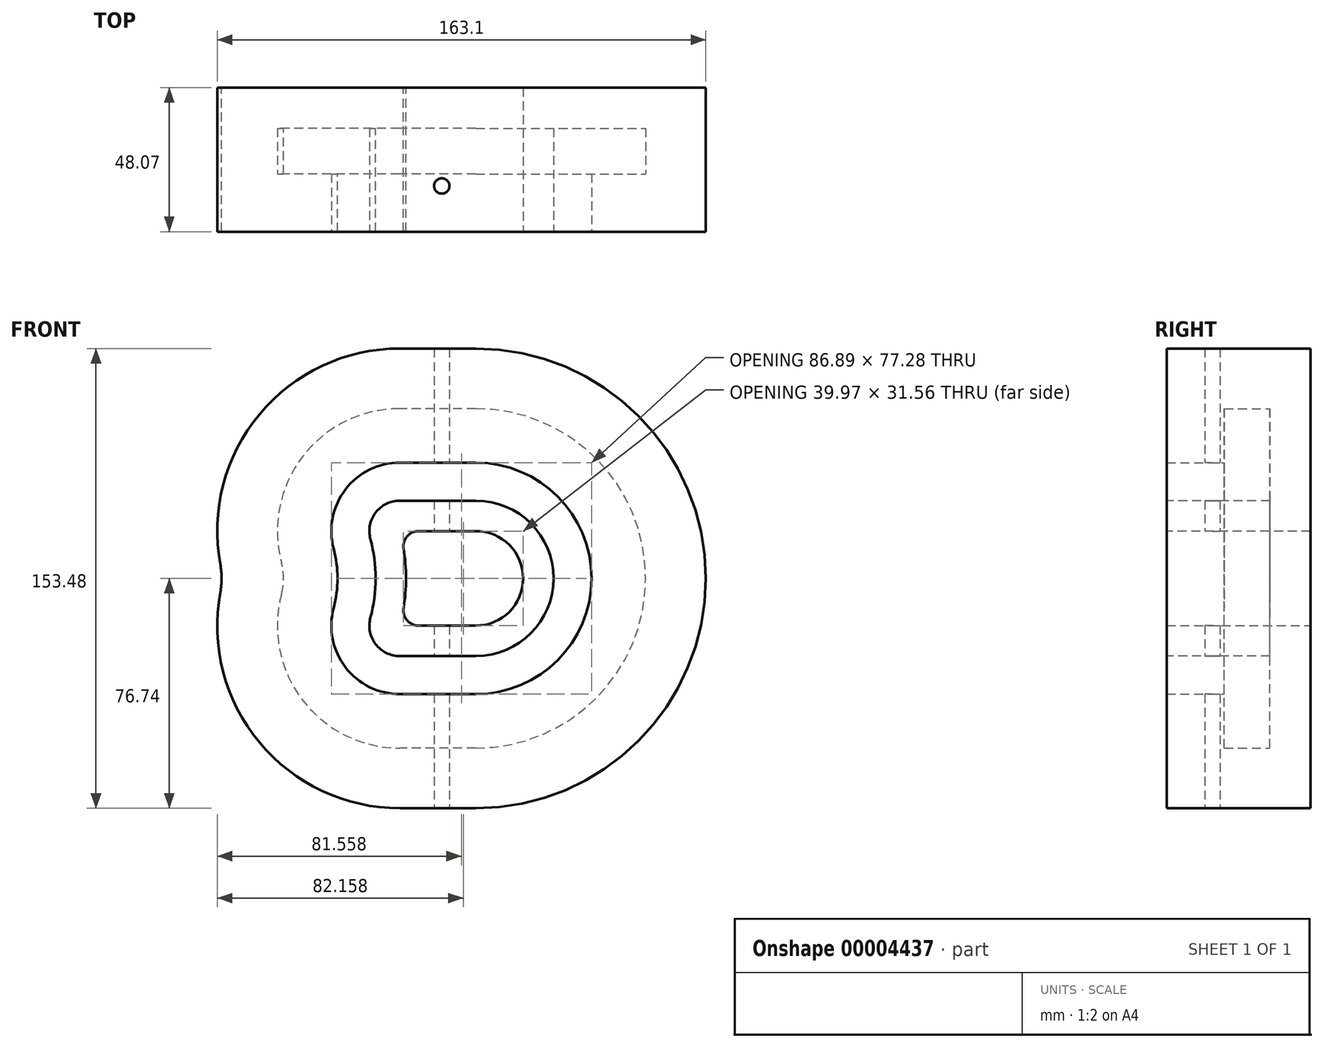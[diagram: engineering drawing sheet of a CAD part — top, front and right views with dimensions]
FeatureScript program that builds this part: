
annotation { "Feature Type Name" : "Feature", "Feature Type Description" : "" }
export const myFeature = defineFeature(function(context is Context, id is Id, definition is map)
    precondition{}
    {
        {
            var Q0;
            Q0=qCreatedBy(makeId("Top.planeOp"),FACE);
            var sketch = newSketch(context, id + "F0", { "sketchPlane" : qUnion([Q0])});
            skLineSegment(sketch, "E0", {"start": v(0, 0) * mm, "end": v(38.1, 0) * mm});
            skLineSegment(sketch, "E1", {"start": v(38.1, 0) * mm, "end": v(38.1, 19.26) * mm});
            skLineSegment(sketch, "E2", {"start": v(38.1, 19.26) * mm, "end": v(20.08, 19.26) * mm});
            skLineSegment(sketch, "E3", {"start": v(20.08, 19.26) * mm, "end": v(20.08, 34.5) * mm});
            skLineSegment(sketch, "E4", {"start": v(20.08, 34.5) * mm, "end": v(50.8, 34.5) * mm});
            skLineSegment(sketch, "E5", {"start": v(50.8, 34.5) * mm, "end": v(50.8, 0) * mm});
            skLineSegment(sketch, "E6", {"start": v(50.8, 0) * mm, "end": v(60.96, 0) * mm});
            skLineSegment(sketch, "E7", {"start": v(60.96, 0) * mm, "end": v(60.96, 48.07) * mm});
            skLineSegment(sketch, "E8", {"start": v(60.96, 48.07) * mm, "end": v(0, 48.07) * mm});
            skLineSegment(sketch, "E9", {"start": v(0, 48.07) * mm, "end": v(0, 0) * mm});
            skSolve(sketch);
        }
        {
            var Q0;
            Q0=makeQuery(id+"F0.imprint","IMPRINT",FACE,{"disambiguationData":[TD([[makeQuery(id+"F0.imprint","IMPRINT",EDGE,{"derivedFrom":sQuery(id+"F0.wireOp",EDGE,"E0")}),1.0]])]});
            var Q1;
            Q1=sQuery(id+"F0.wireOp",EDGE,"E9");
            revolve(context, id + "F1", {"entities" : qUnion([Q0]), "axis" : qUnion([Q1]), "revolveType" : RevolveType.SYMMETRIC, "angle" : 30 * degree});
        }
        {
            var Q0;
            Q0=makeQuery(id+"F1.opRevolve","CAP_FACE",FACE,{"disambiguationData":[OSD([sQuery(id+"F0.wireOp",EDGE,"E0"),sQuery(id+"F0.wireOp",EDGE,"E1"),sQuery(id+"F0.wireOp",EDGE,"E2"),sQuery(id+"F0.wireOp",EDGE,"E3"),sQuery(id+"F0.wireOp",EDGE,"E4"),sQuery(id+"F0.wireOp",EDGE,"E5"),sQuery(id+"F0.wireOp",EDGE,"E6"),sQuery(id+"F0.wireOp",EDGE,"E7"),sQuery(id+"F0.wireOp",EDGE,"E8"),sQuery(id+"F0.wireOp",EDGE,"E9")])],"isStart":false});
            var Q1;
            Q1=makeQuery(id+"F1.opRevolve","CAP_EDGE",EDGE,{"disambiguationData":[OSD([sQuery(id+"F0.wireOp",EDGE,"E7")])],"isStart":false});
            revolve(context, id + "F2", {"operationType" : NewBodyOperationType.ADD, "entities" : qUnion([Q0]), "axis" : qUnion([Q1]), "revolveType" : RevolveType.ONE_DIRECTION, "angle" : 105 * degree});
        }
        {
            var Q0;
            Q0=makeQuery(id+"F1.opRevolve","CAP_FACE",FACE,{"disambiguationData":[OSD([sQuery(id+"F0.wireOp",EDGE,"E0"),sQuery(id+"F0.wireOp",EDGE,"E1"),sQuery(id+"F0.wireOp",EDGE,"E2"),sQuery(id+"F0.wireOp",EDGE,"E3"),sQuery(id+"F0.wireOp",EDGE,"E4"),sQuery(id+"F0.wireOp",EDGE,"E5"),sQuery(id+"F0.wireOp",EDGE,"E6"),sQuery(id+"F0.wireOp",EDGE,"E7"),sQuery(id+"F0.wireOp",EDGE,"E8"),sQuery(id+"F0.wireOp",EDGE,"E9")])],"isStart":true});
            var Q1;
            Q1=makeQuery(id+"F1.opRevolve","CAP_EDGE",EDGE,{"disambiguationData":[OSD([sQuery(id+"F0.wireOp",EDGE,"E7")])],"isStart":true});
            revolve(context, id + "F3", {"operationType" : NewBodyOperationType.ADD, "entities" : qUnion([Q0]), "axis" : qUnion([Q1]), "revolveType" : RevolveType.ONE_DIRECTION, "oppositeDirection" : true, "angle" : 105 * degree});
        }
        {
            var Q0;
            {var subQ0=sQuery(id+"F0.wireOp",EDGE,"E9");Q0=makeQuery(id+"F3.boolean.opBoolean","MERGE",EDGE,{"derivedFrom":[makeQuery(id+"F2.boolean.opBoolean","MERGE",EDGE,{"derivedFrom":[makeQuery(id+"F1.opRevolve","CAP_EDGE",EDGE,{"disambiguationData":[OSD([subQ0])],"isStart":true}),makeQuery(id+"F2.opRevolve","CAP_EDGE",EDGE,{"disambiguationData":[OSD([subQ0])],"isStart":true})]}),makeQuery(id+"F3.opRevolve","CAP_EDGE",EDGE,{"disambiguationData":[OSD([subQ0])],"isStart":true})]});}
            fillet(context, id + "F4", {"entities" : qUnion([Q0]), "radius" : 25.4 * mm, "tangentPropagation" : true, "allowEdgeOverflow" : false});
        }
        {
            var Q0;
            Q0=makeQuery(id+"F3.opRevolve","CAP_FACE",FACE,{"disambiguationData":[OSD([sQuery(id+"F0.wireOp",EDGE,"E0"),sQuery(id+"F0.wireOp",EDGE,"E1"),sQuery(id+"F0.wireOp",EDGE,"E2"),sQuery(id+"F0.wireOp",EDGE,"E3"),sQuery(id+"F0.wireOp",EDGE,"E4"),sQuery(id+"F0.wireOp",EDGE,"E5"),sQuery(id+"F0.wireOp",EDGE,"E6"),sQuery(id+"F0.wireOp",EDGE,"E7"),sQuery(id+"F0.wireOp",EDGE,"E8"),sQuery(id+"F0.wireOp",EDGE,"E9")])],"isStart":false});
            var Q1;
            Q1=makeQuery(id+"F2.opRevolve","CAP_FACE",FACE,{"disambiguationData":[OSD([sQuery(id+"F0.wireOp",EDGE,"E0"),sQuery(id+"F0.wireOp",EDGE,"E1"),sQuery(id+"F0.wireOp",EDGE,"E2"),sQuery(id+"F0.wireOp",EDGE,"E3"),sQuery(id+"F0.wireOp",EDGE,"E4"),sQuery(id+"F0.wireOp",EDGE,"E5"),sQuery(id+"F0.wireOp",EDGE,"E6"),sQuery(id+"F0.wireOp",EDGE,"E7"),sQuery(id+"F0.wireOp",EDGE,"E8"),sQuery(id+"F0.wireOp",EDGE,"E9")])],"isStart":false});
            extrude(context, id + "F5", {"entities" : qUnion([Q0, Q1]), "operationType" : NewBodyOperationType.ADD, "depth" : 25.4 * mm});
        }
        {
            var Q0;
            {var subQ0=sQuery(id+"F0.wireOp",EDGE,"E7");var subQ1=makeQuery(id+"F3.boolean.opBoolean","MERGE",EDGE,{"derivedFrom":[makeQuery(id+"F1.opRevolve","CAP_EDGE",EDGE,{"disambiguationData":[OSD([subQ0])],"isStart":true}),makeQuery(id+"F3.opRevolve","CAP_EDGE",EDGE,{"disambiguationData":[OSD([subQ0])],"isStart":true})]});Q0=makeQuery(id+"F5.boolean.opBoolean","MERGE",EDGE,{"derivedFrom":[subQ1,makeQuery(id+"F5.opExtrude","CAP_EDGE",EDGE,{"disambiguationData":[OSD([subQ0]),TDD([subQ1])],"isStart":true})]});}
            var Q1;
            {var subQ0=sQuery(id+"F0.wireOp",EDGE,"E7");var subQ1=makeQuery(id+"F2.boolean.opBoolean","MERGE",EDGE,{"derivedFrom":[makeQuery(id+"F1.opRevolve","CAP_EDGE",EDGE,{"disambiguationData":[OSD([subQ0])],"isStart":false}),makeQuery(id+"F2.opRevolve","CAP_EDGE",EDGE,{"disambiguationData":[OSD([subQ0])],"isStart":true})]});Q1=makeQuery(id+"F5.boolean.opBoolean","MERGE",EDGE,{"derivedFrom":[subQ1,makeQuery(id+"F5.opExtrude","CAP_EDGE",EDGE,{"disambiguationData":[OSD([subQ0]),TDD([subQ1])],"isStart":true})]});}
            fillet(context, id + "F6", {"entities" : qUnion([Q0, Q1]), "radius" : 5.08 * mm, "tangentPropagation" : true, "allowEdgeOverflow" : false});
        }
        {
            var Q0;
            {var subQ0=sQuery(id+"F0.wireOp",EDGE,"E0");var subQ1=sQuery(id+"F0.wireOp",EDGE,"E1");var subQ2=sQuery(id+"F0.wireOp",EDGE,"E2");var subQ3=sQuery(id+"F0.wireOp",EDGE,"E3");var subQ4=sQuery(id+"F0.wireOp",EDGE,"E4");var subQ5=sQuery(id+"F0.wireOp",EDGE,"E5");var subQ6=sQuery(id+"F0.wireOp",EDGE,"E6");var subQ7=sQuery(id+"F0.wireOp",EDGE,"E7");var subQ8=sQuery(id+"F0.wireOp",EDGE,"E8");var subQ9=sQuery(id+"F0.wireOp",EDGE,"E9");Q0=makeQuery(id+"F5.opExtrude","CAP_FACE",FACE,{"disambiguationData":[OSD([subQ0,subQ1,subQ2,subQ3,subQ4,subQ5,subQ6,subQ7,subQ8,subQ9]),TDD([makeQuery(id+"F2.opRevolve","CAP_FACE",FACE,{"disambiguationData":[OSD([subQ0,subQ1,subQ2,subQ3,subQ4,subQ5,subQ6,subQ7,subQ8,subQ9])],"isStart":false})])],"isStart":false});}
            var sketch = newSketch(context, id + "F7", { "sketchPlane" : qUnion([Q0])});
            skLineSegment(sketch, "E10", {"start": v(0, 0) * mm, "end": v(61.35, 0) * mm});
            skLineSegment(sketch, "E11.0.0", {"start": v(48.07, 76.74) * mm, "end": v(0, 76.74) * mm});
            skLineSegment(sketch, "E11.0.1", {"start": v(0, 76.74) * mm, "end": v(0, 38.64) * mm});
            skLineSegment(sketch, "E11.0.2", {"start": v(0, 38.64) * mm, "end": v(19.26, 38.64) * mm});
            skLineSegment(sketch, "E11.0.3", {"start": v(19.26, 38.64) * mm, "end": v(19.26, 56.66) * mm});
            skLineSegment(sketch, "E11.0.4", {"start": v(19.26, 56.66) * mm, "end": v(34.5, 56.66) * mm});
            skLineSegment(sketch, "E11.0.5", {"start": v(34.5, 56.66) * mm, "end": v(34.5, 25.94) * mm});
            skLineSegment(sketch, "E11.0.6", {"start": v(34.5, 25.94) * mm, "end": v(0, 25.94) * mm});
            skLineSegment(sketch, "E11.0.7", {"start": v(0, 25.94) * mm, "end": v(0, 15.78) * mm});
            skLineSegment(sketch, "E11.0.8", {"start": v(0, 15.78) * mm, "end": v(48.07, 15.78) * mm});
            skLineSegment(sketch, "E11.0.9", {"start": v(48.07, 15.78) * mm, "end": v(48.07, 76.74) * mm});
            skSolve(sketch);
        }
        {
            var Q0;
            Q0 = qSketchRegion(id + "F7", true);
            var Q1;
            Q1=sQuery(id+"F7.wireOp",EDGE,"E10");
            revolve(context, id + "F8", {"operationType" : NewBodyOperationType.ADD, "entities" : qUnion([Q0]), "axis" : qUnion([Q1]), "revolveType" : RevolveType.ONE_DIRECTION, "angle" : 180 * degree});
        }
        {
            var Q0;
            {var subQ0=sQuery(id+"F0.wireOp",EDGE,"E9");Q0=makeQuery(id+"F5.opExtrude","SWEPT_FACE",FACE,{"disambiguationData":[OSD([subQ0]),TDD([makeQuery(id+"F3.opRevolve","CAP_EDGE",EDGE,{"disambiguationData":[OSD([subQ0])],"isStart":false})])]});}
            var sketch = newSketch(context, id + "F9", { "sketchPlane" : qUnion([Q0])});
            skCircle(sketch, "E12", {"center": v(72.9, -15.25) * mm, "radius": 2.55 * mm});
            skSolve(sketch);
        }
        {
            var Q0;
            Q0 = qSketchRegion(id + "F9", true);
            extrude(context, id + "F10", {"entities" : qUnion([Q0]), "operationType" : NewBodyOperationType.REMOVE, "endBound" : BoundingType.THROUGH_ALL, "oppositeDirection" : true, "depth" : 25.4 * mm});
        }
    });
